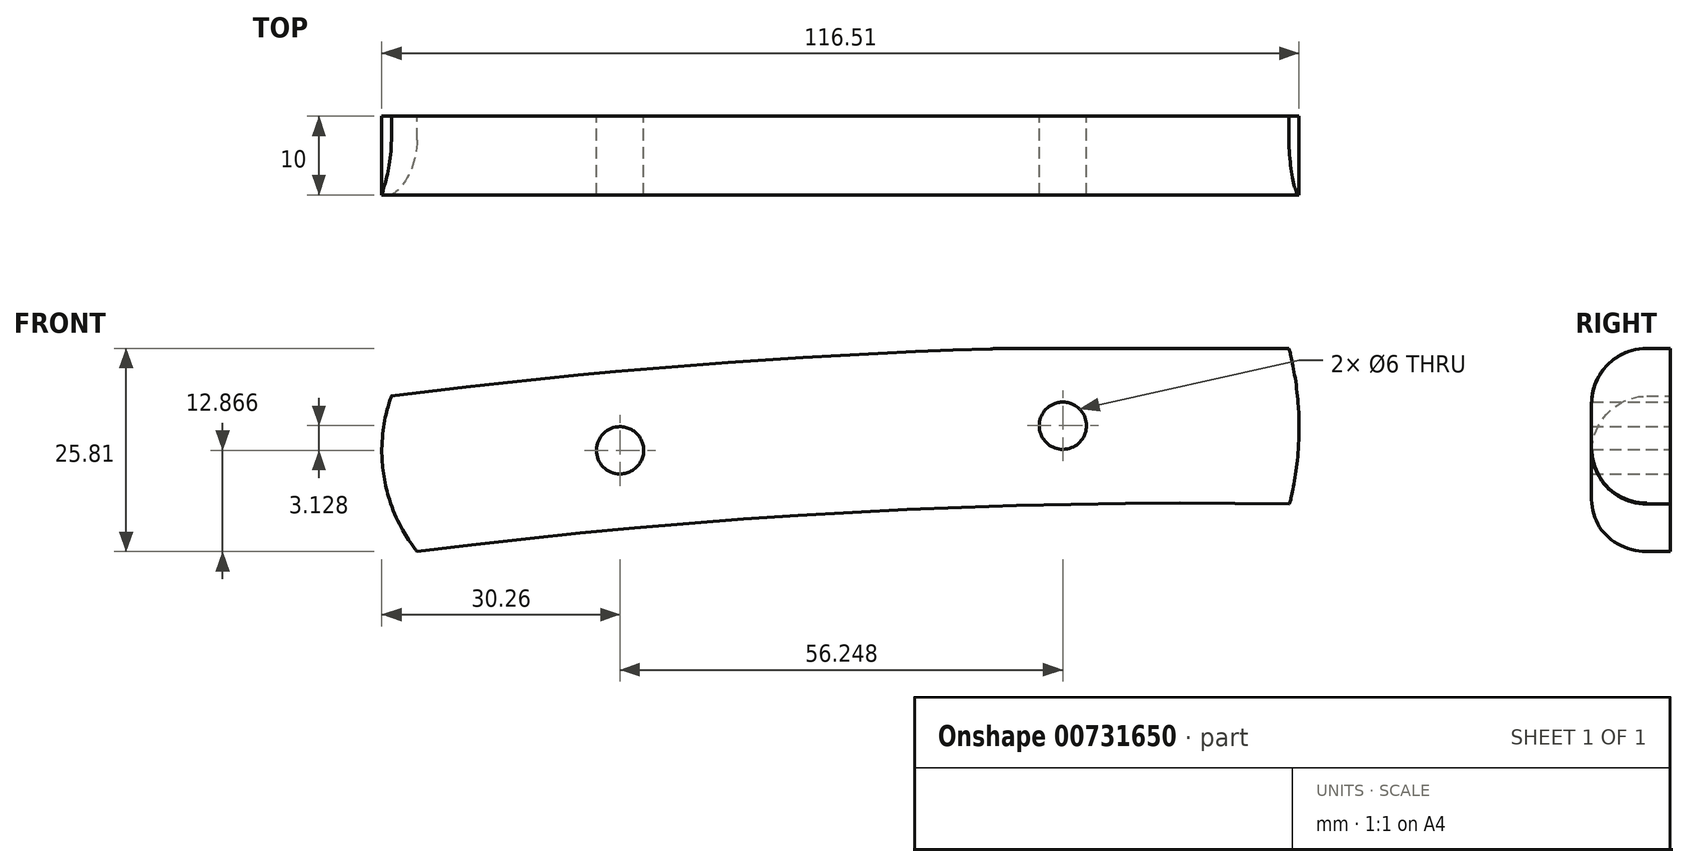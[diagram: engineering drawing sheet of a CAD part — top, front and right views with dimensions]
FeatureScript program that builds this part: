
annotation { "Feature Type Name" : "Feature", "Feature Type Description" : "" }
export const myFeature = defineFeature(function(context is Context, id is Id, definition is map)
    precondition{}
    {
        {
            var Q0;
            Q0=qCreatedBy(makeId("Front.planeOp"),FACE);
            var sketch = newSketch(context, id + "F0", { "sketchPlane" : qUnion([Q0])});
            skArc(sketch, "E0.0", {"start": v(13.6, 9.05) * mm, "mid": v(-24.53, 6.95) * mm, "end": v(-62.51, 3.04) * mm});
            skArc(sketch, "E1.0", {"start": v(16.72, 9.1) * mm, "mid": v(15.16, 9.09) * mm, "end": v(13.6, 9.05) * mm});
            skLineSegment(sketch, "E2.0", {"start": v(16.72, 9.1) * mm, "end": v(51.52, 9.1) * mm});
            skCircle(sketch, "E3.0", {"center": v(22.79, -0.72) * mm, "radius": 3 * mm});
            skCircle(sketch, "E4.0", {"center": v(-33.46, -3.84) * mm, "radius": 3 * mm});
            skArc(sketch, "E5.0", {"start": v(51.58, -10.67) * mm, "mid": v(-3.93, -11.72) * mm, "end": v(-59.23, -16.7) * mm});
            skArc(sketch, "E6.0", {"start": v(-62.51, 3.04) * mm, "mid": v(-63.44, -7.26) * mm, "end": v(-59.23, -16.7) * mm});
            skArc(sketch, "E7.0", {"start": v(51.58, -10.67) * mm, "mid": v(52.79, -0.78) * mm, "end": v(51.52, 9.1) * mm});
            skSolve(sketch);
        }
        {
            var Q0;
            Q0=makeQuery(id+"F0.imprint","IMPRINT",FACE,{"disambiguationData":[TD([[makeQuery(id+"F0.imprint","IMPRINT",EDGE,{"derivedFrom":sQuery(id+"F0.wireOp",EDGE,"E0.0")}),1.0]])]});
            extrude(context, id + "F1", {"entities" : qUnion([Q0]), "depth" : 10 * mm, "offsetDistance" : 25 * mm});
        }
        {
            var Q0;
            Q0=makeQuery(id+"F1.opExtrude","CAP_EDGE",EDGE,{"disambiguationData":[OSD([sQuery(id+"F0.wireOp",EDGE,"E0.0")])],"isStart":false});
            var Q1;
            Q1=makeQuery(id+"F1.opExtrude","CAP_EDGE",EDGE,{"disambiguationData":[OSD([sQuery(id+"F0.wireOp",EDGE,"E5.0")])],"isStart":false});
            fillet(context, id + "F2", {"entities" : qUnion([Q0, Q1]), "radius" : 7 * mm, "tangentPropagation" : true, "allowEdgeOverflow" : false});
        }
    });
